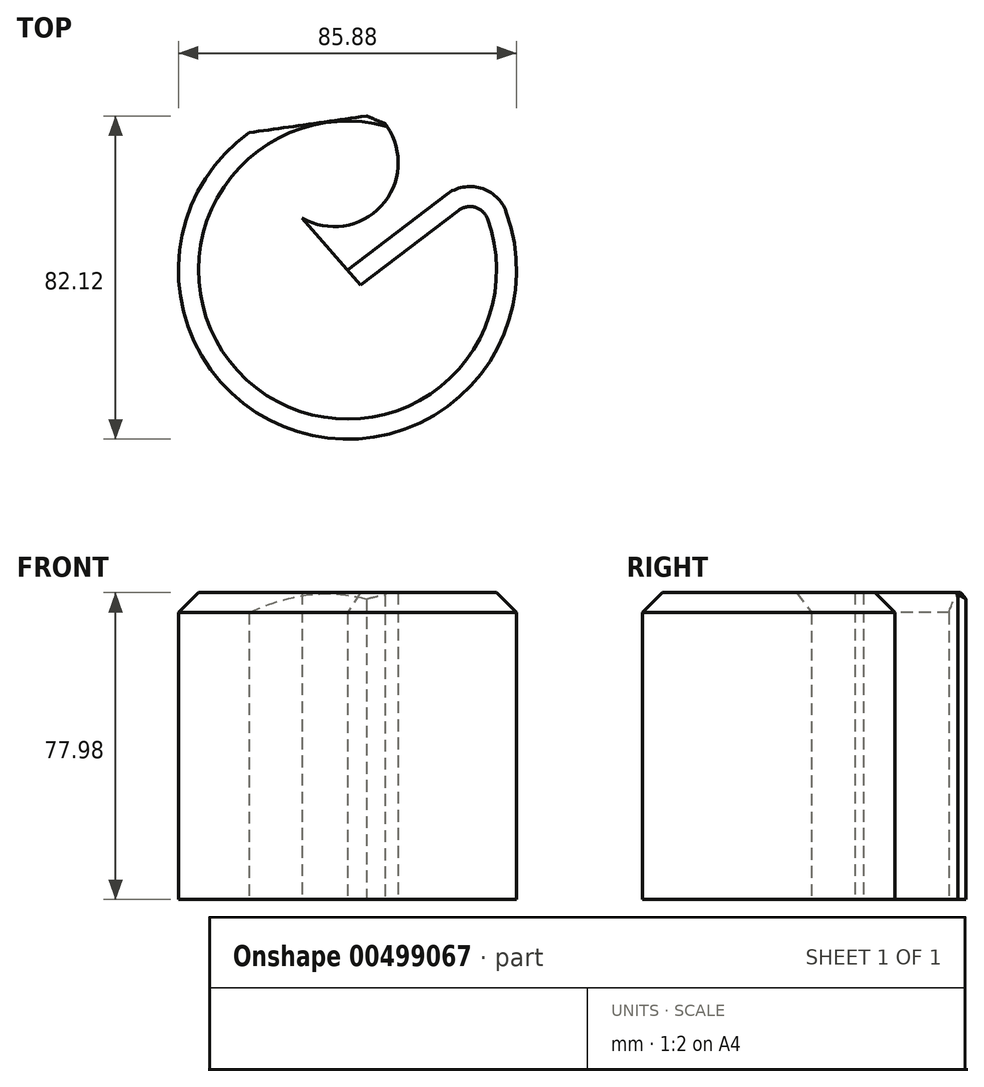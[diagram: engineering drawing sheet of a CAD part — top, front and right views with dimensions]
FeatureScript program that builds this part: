
annotation { "Feature Type Name" : "Feature", "Feature Type Description" : "" }
export const myFeature = defineFeature(function(context is Context, id is Id, definition is map)
    precondition{}
    {
        {
            var Q0;
            Q0=qCreatedBy(makeId("Top.planeOp"),FACE);
            var sketch = newSketch(context, id + "F0", { "sketchPlane" : qUnion([Q0])});
            skArc(sketch, "E0", {"start": v(-39.8, 38.6) * mm, "mid": v(-21.17, -38.8) * mm, "end": v(19.3, 29.75) * mm});
            skArc(sketch, "E1", {"start": v(-26.33, 16.89) * mm, "mid": v(-5, 21.52) * mm, "end": v(-7.44, 43.22) * mm});
            skLineSegment(sketch, "E2", {"start": v(-39.8, 38.6) * mm, "end": v(-7.44, 43.22) * mm});
            skLineSegment(sketch, "E3", {"start": v(-26.33, 16.89) * mm, "end": v(-14.82, 3.68) * mm});
            skLineSegment(sketch, "E4", {"start": v(19.3, 29.75) * mm, "end": v(-14.82, 3.68) * mm});
            skSolve(sketch);
        }
        {
            var Q0;
            Q0=makeQuery(id+"F0.imprint","IMPRINT",FACE,{"disambiguationData":[TD([[makeQuery(id+"F0.imprint","IMPRINT",EDGE,{"derivedFrom":sQuery(id+"F0.wireOp",EDGE,"E0")}),1.0]])]});
            extrude(context, id + "F1", {"entities" : qUnion([Q0]), "depth" : 77.98 * mm});
        }
        {
            var Q0;
            Q0=makeQuery(id+"F1.opExtrude","SWEPT_EDGE",EDGE,{"disambiguationData":[OSD([sQuery(id+"F0.wireOp",EDGE,"E0"),sQuery(id+"F0.wireOp",EDGE,"E4")])]});
            fillet(context, id + "F2", {"entities" : qUnion([Q0]), "radius" : 9.8 * mm, "tangentPropagation" : true, "allowEdgeOverflow" : false});
        }
        {
            var Q0;
            Q0=makeQuery(id+"F1.opExtrude","SWEPT_EDGE",EDGE,{"disambiguationData":[OSD([sQuery(id+"F0.wireOp",EDGE,"E1"),sQuery(id+"F0.wireOp",EDGE,"E2")])]});
            chamfer(context, id + "F3", {"entities" : qUnion([Q0]), "width" : 5.08 * mm, "tangentPropagation" : true});
        }
        {
            var Q0;
            Q0=makeQuery(id+"F1.opExtrude","CAP_EDGE",EDGE,{"disambiguationData":[OSD([sQuery(id+"F0.wireOp",EDGE,"E0")])],"isStart":false});
            chamfer(context, id + "F4", {"entities" : qUnion([Q0]), "width" : 5.08 * mm, "tangentPropagation" : true});
        }
    });
